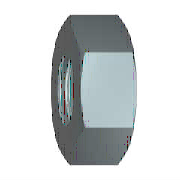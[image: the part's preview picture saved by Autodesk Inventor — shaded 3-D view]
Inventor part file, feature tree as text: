
AUTODESK INVENTOR PART (.ipt)
format: ipt  version: 2024.3 (Build 283343000, 343)  size: 161,280 bytes
history: native  units: mm (DEFAULTED — no unit token found)
features: chamfer x1, hole x1, other x1, plane x1
ambient origin geometry x7: Origin, YZ Plane, XZ Plane, X Axis, Y Axis, Z Axis, Center Point
bodies: Solid1 (feature_tree), Body (feature_tree)
feature tree (4):
  chamfer  "Chamfer1"  Distance=15.011107mm
  hole  "Thread"  [1 undecoded]
  other  "Work Axis1"
  plane  "Work Plane1"
note: 1 required parameter value undecoded (feature->parameter linkage not recoverable at this tier; creation-order binding heuristic only, values carry confidence <= 0.55)
